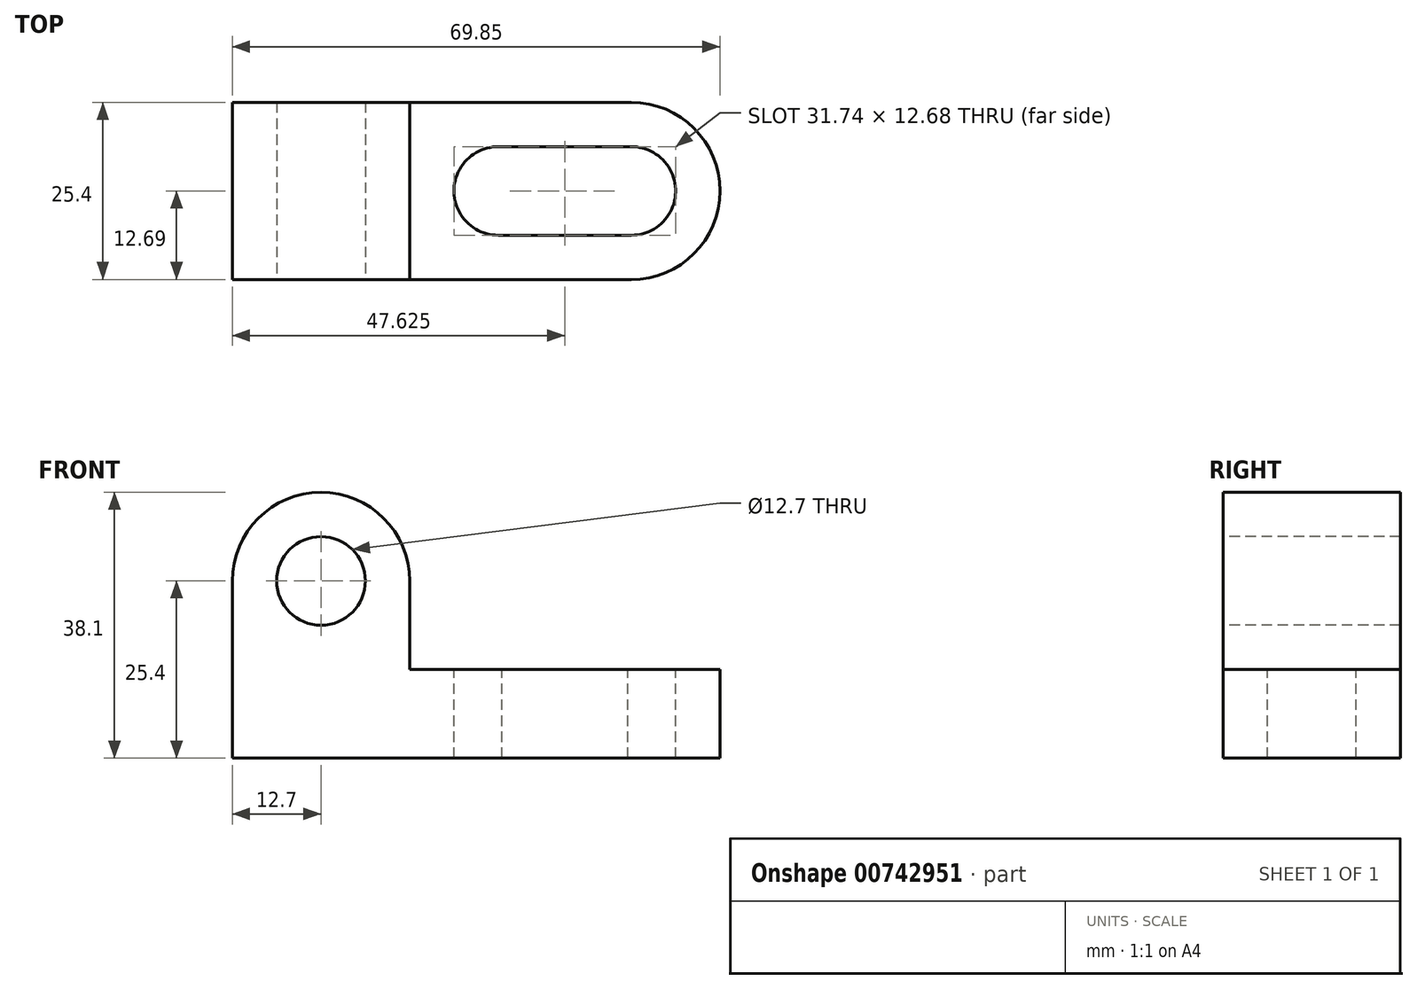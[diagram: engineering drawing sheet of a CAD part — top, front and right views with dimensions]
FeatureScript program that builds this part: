
annotation { "Feature Type Name" : "Feature", "Feature Type Description" : "" }
export const myFeature = defineFeature(function(context is Context, id is Id, definition is map)
    precondition{}
    {
        {
            var Q0;
            Q0=qCreatedBy(makeId("Front.planeOp"),FACE);
            var sketch = newSketch(context, id + "F0", { "sketchPlane" : qUnion([Q0])});
            skLineSegment(sketch, "E0", {"start": v(0, 0) * mm, "end": v(69.85, 0) * mm});
            skLineSegment(sketch, "E1", {"start": v(0, 0) * mm, "end": v(0, 38.1) * mm});
            skLineSegment(sketch, "E2", {"start": v(0, 38.1) * mm, "end": v(69.85, 38.1) * mm});
            skLineSegment(sketch, "E3", {"start": v(69.85, 38.1) * mm, "end": v(69.85, 0) * mm});
            skSolve(sketch);
        }
        {
            var Q0;
            Q0 = qSketchRegion(id + "F0", true);
            extrude(context, id + "F1", {"entities" : qUnion([Q0]), "depth" : 25.4 * mm, "offsetDistance" : 25.4 * mm});
        }
        {
            var Q0;
            Q0=makeQuery(id+"F1.opExtrude","CAP_FACE",FACE,{"disambiguationData":[OSD([sQuery(id+"F0.wireOp",EDGE,"E0"),sQuery(id+"F0.wireOp",EDGE,"E1"),sQuery(id+"F0.wireOp",EDGE,"E2"),sQuery(id+"F0.wireOp",EDGE,"E3")])],"isStart":false});
            var sketch = newSketch(context, id + "F2", { "sketchPlane" : qUnion([Q0])});
            skLineSegment(sketch, "E4.bottom", {"start": v(25.4, 38.1) * mm, "end": v(69.85, 38.1) * mm});
            skLineSegment(sketch, "E4.top", {"start": v(25.4, 12.7) * mm, "end": v(69.85, 12.7) * mm});
            skLineSegment(sketch, "E4.left", {"start": v(25.4, 38.1) * mm, "end": v(25.4, 12.7) * mm});
            skLineSegment(sketch, "E4.right", {"start": v(69.85, 38.1) * mm, "end": v(69.85, 12.7) * mm});
            skSolve(sketch);
        }
        {
            var Q0;
            Q0 = qSketchRegion(id + "F2", true);
            extrude(context, id + "F3", {"entities" : qUnion([Q0]), "operationType" : NewBodyOperationType.REMOVE, "oppositeDirection" : true, "depth" : 25.4 * mm, "offsetDistance" : 25.4 * mm});
        }
        {
            var Q0;
            Q0=makeQuery(id+"F1.opExtrude","CAP_FACE",FACE,{"disambiguationData":[OSD([sQuery(id+"F0.wireOp",EDGE,"E0"),sQuery(id+"F0.wireOp",EDGE,"E1"),sQuery(id+"F0.wireOp",EDGE,"E2"),sQuery(id+"F0.wireOp",EDGE,"E3")])],"isStart":false});
            var sketch = newSketch(context, id + "F4", { "sketchPlane" : qUnion([Q0])});
            skArc(sketch, "E5", {"start": v(25.4, 25.4) * mm, "mid": v(12.7, 38.1) * mm, "end": v(0, 25.4) * mm});
            skCircle(sketch, "E6", {"center": v(12.7, 25.4) * mm, "radius": 6.35 * mm});
            skLineSegment(sketch, "E7", {"start": v(0, 25.4) * mm, "end": v(0, 38.1) * mm});
            skLineSegment(sketch, "E8", {"start": v(0, 38.1) * mm, "end": v(25.4, 38.1) * mm});
            skLineSegment(sketch, "E9", {"start": v(25.4, 38.1) * mm, "end": v(25.4, 25.4) * mm});
            skSolve(sketch);
        }
        {
            var Q0;
            Q0 = qSketchRegion(id + "F4", true);
            extrude(context, id + "F5", {"entities" : qUnion([Q0]), "operationType" : NewBodyOperationType.REMOVE, "oppositeDirection" : true, "depth" : 25.4 * mm, "offsetDistance" : 25.4 * mm});
        }
        {
            var Q0;
            Q0=makeQuery(id+"F3.boolean.opBoolean","COPY",FACE,{"derivedFrom":makeQuery(id+"F3.opExtrude","SWEPT_FACE",FACE,{"disambiguationData":[OSD([sQuery(id+"F2.wireOp",EDGE,"E4.top")])]})});
            var sketch = newSketch(context, id + "F6", { "sketchPlane" : qUnion([Q0])});
            skArc(sketch, "E10", {"start": v(57.15, -25.4) * mm, "mid": v(69.85, -12.7) * mm, "end": v(57.15, 0) * mm});
            skLineSegment(sketch, "E11", {"start": v(57.15, 0) * mm, "end": v(69.85, 0) * mm});
            skLineSegment(sketch, "E12", {"start": v(69.85, 0) * mm, "end": v(69.85, -25.4) * mm});
            skLineSegment(sketch, "E13", {"start": v(69.85, -25.4) * mm, "end": v(57.15, -25.4) * mm});
            skCircle(sketch, "E14", {"center": v(57.15, -12.7) * mm, "radius": 6.35 * mm});
            skCircle(sketch, "E15", {"center": v(38.1, -12.7) * mm, "radius": 6.35 * mm});
            skLineSegment(sketch, "E16", {"start": v(57.66, -6.37) * mm, "end": v(37.59, -6.37) * mm});
            skLineSegment(sketch, "E17", {"start": v(38.1, -19.05) * mm, "end": v(57.15, -19.05) * mm});
            skSolve(sketch);
        }
        {
            var Q0;
            Q0 = qSketchRegion(id + "F6", true);
            extrude(context, id + "F7", {"entities" : qUnion([Q0]), "operationType" : NewBodyOperationType.REMOVE, "oppositeDirection" : true, "depth" : 25.4 * mm, "offsetDistance" : 25.4 * mm});
        }
    });
